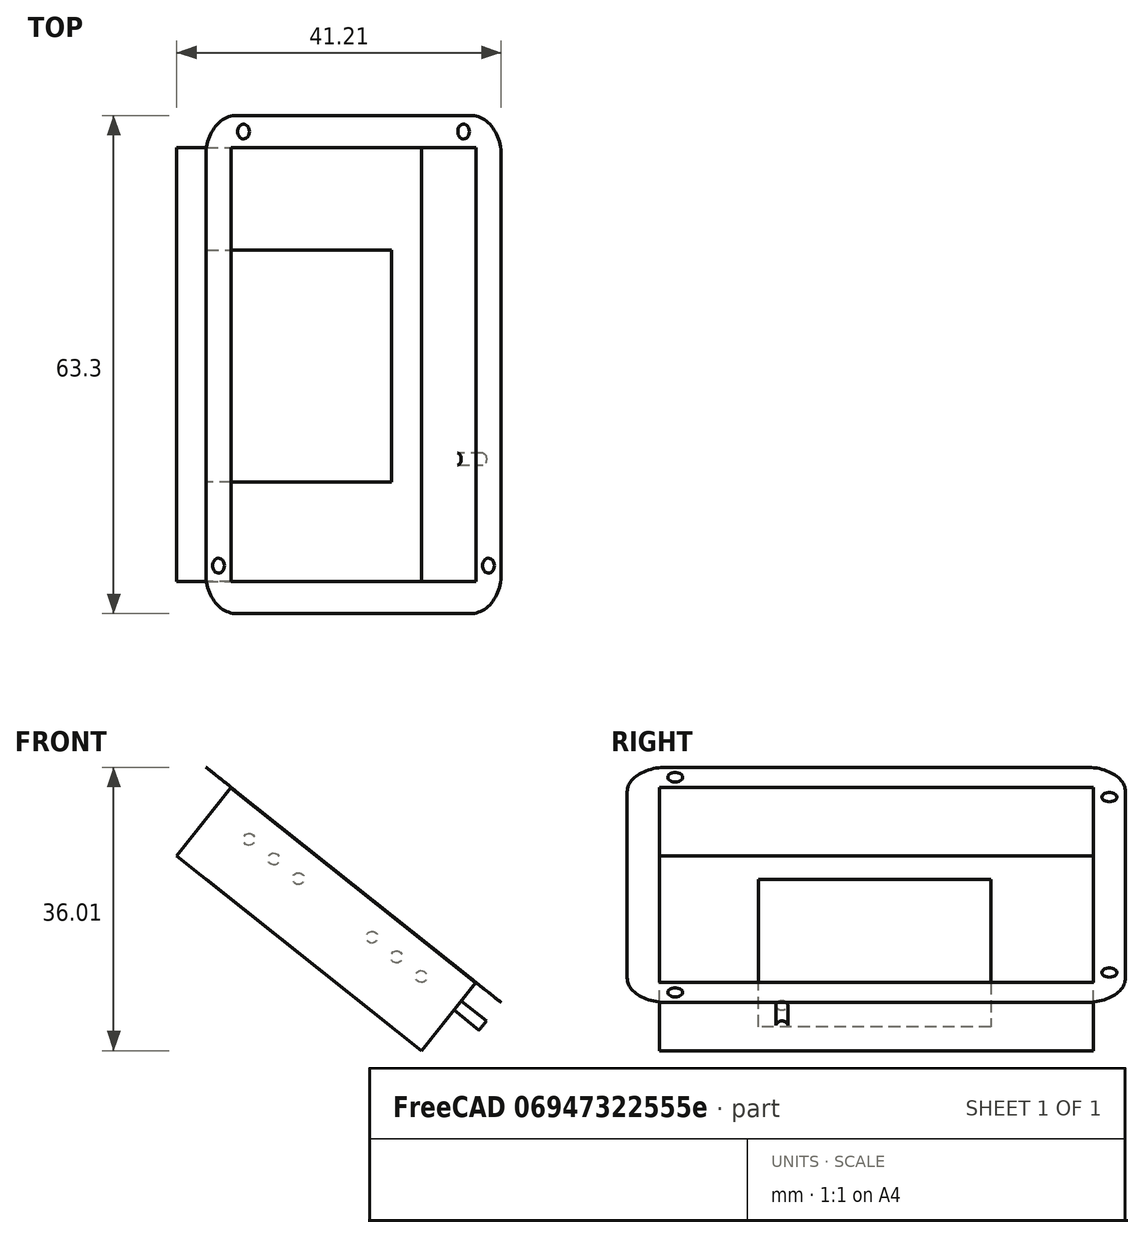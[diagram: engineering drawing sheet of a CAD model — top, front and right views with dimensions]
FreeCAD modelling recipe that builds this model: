
FCSTD DOCUMENT  (FreeCAD 0.20R29410 (Git))
Label: sensor-assembly3
License: All rights reserved
LicenseURL: http://en.wikipedia.org/wiki/All_rights_reserved
objects: Part::FeaturePython×32, App::FeaturePython×17, App::Link×3
note: 31 computed .brp shape members not serialized (recipe doc carries the construction recipe); baked Part::Feature solids carry a one-line shape summary decoded from their .brp
EXTERNAL_REF file=enclosure.FCStd obj=Link
EXTERNAL_REF file=electronics.FCStd obj=Link
EXTERNAL_REF file=cover.FCStd obj=Link

FEATURE [App::Link] Link002  label="enclosure"
  LinkPlacement = pos=(-20.5515,-30.0951,-26.6981) rot=(0,1,0;0.672893rad)
  LinkedObject = -> <external enclosure.FCStd>#Link
  Placement = pos=(-20.5515,-30.0951,-26.6981) rot=(0,1,0;0.672893rad)
  _LinkOwner = 81
FEATURE [App::Link] Link004  label="electronics"
  LinkPlacement = pos=(-19.9282,-30.0951,-25.9161) rot=(0,1,0;0.672893rad)
  LinkedObject = -> <external electronics.FCStd>#Link
  Placement = pos=(-19.9282,-30.0951,-25.9161) rot=(0,1,0;0.672893rad)
  _LinkOwner = 81
FEATURE [App::Link] Link  label="cover"
  LinkPlacement = pos=(-3.91067,-30.0951,-5.81815) rot=(0,-1,0;2.4687rad)
  LinkedObject = -> <external cover.FCStd>#Link
  Placement = pos=(-3.91067,-30.0951,-5.81815) rot=(0,-1,0;2.4687rad)
  _LinkOwner = 81
FEATURE [Part::FeaturePython] Parts  # WARN: FeaturePython — macro-defined, semantics opaque (R4)
  Group = -> [Link002,Link004,Link]
  GroupMode = 0
FEATURE [Part::FeaturePython] Assembly  label="Assembly3"  # WARN: FeaturePython — macro-defined, semantics opaque (R4)
  AutoRelax = true
  BuildShape = 0
  Freeze = false
  Group = -> [Constraints,Elements,Parts]
  Verbose = false
  _SolverType = 1
  _Version = 1
FEATURE [App::FeaturePython] Constraints  # WARN: FeaturePython — macro-defined, semantics opaque (R4)
  Group = -> [Constraint,Constraint001,Constraint002,Constraint003,Constraint004]
  _Version = 1
FEATURE [App::FeaturePython] Elements  # WARN: FeaturePython — macro-defined, semantics opaque (R4)
  Group = -> [_Element001,_Element003,_Element006,_Element008,_Element019,_Element021,_Element023,_Element024,_Element026,_Element028,_Element029,_Element031,_Element032,_Element034,_Element035,_Element036,_Element037,_Element038,_Element039,_Element040,_Element041,_Element042,_Element,_Element043,_Element044,_Element045,_Element046,_Element047,_Element048,_Element049]
FEATURE [Part::FeaturePython] _Element001  # link proxy (typed FeaturePython)
  Detach = false
  LinkTransform = true
  LinkedObject = -> Link002 [Pad001.Face15]
  _Parent = -> Elements
FEATURE [Part::FeaturePython] _Element003  # link proxy (typed FeaturePython)
  Detach = false
  LinkTransform = true
  LinkedObject = -> Link002 [Pad001.Face11]
  _Parent = -> Elements
FEATURE [Part::FeaturePython] _Element006  # link proxy (typed FeaturePython)
  Detach = false
  LinkTransform = true
  LinkedObject = -> Link002 [Pad001.Face13]
  _Parent = -> Elements
FEATURE [Part::FeaturePython] _Element008  # link proxy (typed FeaturePython)
  Detach = false
  LinkTransform = true
  LinkedObject = -> Link002 [Pad001.Face12]
  _Parent = -> Elements
FEATURE [Part::FeaturePython] _Element019  # link proxy (typed FeaturePython)
  Detach = false
  LinkTransform = true
  LinkedObject = -> Link002 [Pocket003.Face23]
  _Parent = -> Elements
FEATURE [Part::FeaturePython] _Element021  # link proxy (typed FeaturePython)
  Detach = false
  LinkTransform = true
  LinkedObject = -> Link002 [Pocket003.Vertex53]
  _Parent = -> Elements
FEATURE [Part::FeaturePython] _Element023  # link proxy (typed FeaturePython)
  Detach = false
  LinkTransform = true
  LinkedObject = -> Link002 [Pocket001.Vertex32]
  _Parent = -> Elements
FEATURE [Part::FeaturePython] _Element024  # link proxy (typed FeaturePython)
  Detach = false
  LinkTransform = true
  LinkedObject = -> Link002 [Pocket001.Vertex28]
  _Parent = -> Elements
FEATURE [Part::FeaturePython] _Element026  # link proxy (typed FeaturePython)
  Detach = false
  LinkTransform = true
  LinkedObject = -> Link002 [Pocket001.Vertex31]
  _Parent = -> Elements
FEATURE [Part::FeaturePython] _Element028  # link proxy (typed FeaturePython)
  Detach = false
  LinkTransform = true
  LinkedObject = -> Link002 [Pocket003.Face46]
  _Parent = -> Elements
FEATURE [Part::FeaturePython] _Element029  # link proxy (typed FeaturePython)
  Detach = false
  LinkTransform = true
  LinkedObject = -> Link002 [Pocket003.Vertex25]
  _Parent = -> Elements
FEATURE [Part::FeaturePython] _Element031  # link proxy (typed FeaturePython)
  Detach = false
  LinkTransform = true
  LinkedObject = -> Link002 [Pocket003.Vertex54]
  _Parent = -> Elements
FEATURE [Part::FeaturePython] _Element032  # link proxy (typed FeaturePython)
  Detach = false
  LinkTransform = true
  LinkedObject = -> Link002 [Pocket003.Vertex26]
  _Parent = -> Elements
FEATURE [Part::FeaturePython] _Element034  # link proxy (typed FeaturePython)
  Detach = false
  LinkTransform = true
  LinkedObject = -> Link002 [Pocket003.Vertex55]
  _Parent = -> Elements
FEATURE [Part::FeaturePython] _Element035  # link proxy (typed FeaturePython)
  Detach = false
  LinkTransform = true
  LinkedObject = -> Link004 [Pad.Face5]
  _Parent = -> Elements
FEATURE [Part::FeaturePython] _Element036  # link proxy (typed FeaturePython)
  Detach = false
  LinkTransform = true
  LinkedObject = -> Link002 [Pocket003.Face22]
  _Parent = -> Elements
FEATURE [Part::FeaturePython] _Element037  # link proxy (typed FeaturePython)
  Detach = false
  LinkTransform = true
  LinkedObject = -> Link002 [Pocket003.Vertex57]
  _Parent = -> Elements
FEATURE [Part::FeaturePython] _Element038  # link proxy (typed FeaturePython)
  Detach = false
  LinkTransform = true
  LinkedObject = -> Link004 [Pad.Vertex1]
  _Parent = -> Elements
FEATURE [Part::FeaturePython] _Element039  # link proxy (typed FeaturePython)
  Detach = false
  LinkTransform = true
  LinkedObject = -> Link004 [Pad.Vertex3]
  _Parent = -> Elements
FEATURE [Part::FeaturePython] _Element040  # link proxy (typed FeaturePython)
  Detach = false
  LinkTransform = true
  LinkedObject = -> Link002 [Pocket003.Vertex58]
  _Parent = -> Elements
FEATURE [Part::FeaturePython] _Element041  # link proxy (typed FeaturePython)
  Detach = false
  LinkTransform = true
  LinkedObject = -> Link002 [Pocket003.Face48]
  _Parent = -> Elements
FEATURE [Part::FeaturePython] _Element042  # link proxy (typed FeaturePython)
  Detach = false
  LinkTransform = true
  LinkedObject = -> Link004 [Pad.Face1]
  _Parent = -> Elements
FEATURE [Part::FeaturePython] _Element  # link proxy (typed FeaturePython)
  Detach = false
  LinkTransform = true
  LinkedObject = -> Link004 [Pad.Face3]
  _Parent = -> Elements
FEATURE [App::FeaturePython] Constraint  label="AxialAlignment"  # WARN: FeaturePython — macro-defined, semantics opaque (R4)
  Angle = 0
  AnglePitch = 0
  AngleRoll = 0
  Disabled = false
  Group = -> [ElementLink,ElementLink001]
  LockAngle = false
  Multiply = false
  _ConstraintType = 36
  _Parent = -> Constraints
FEATURE [App::FeaturePython] ElementLink  label="_Element043"  # link proxy (typed FeaturePython)
  LinkTransform = true
  LinkedObject = -> _Element043
  _Parent = -> Constraint
FEATURE [Part::FeaturePython] _Element043  # link proxy (typed FeaturePython)
  Detach = false
  LinkTransform = true
  LinkedObject = -> Link002 [Pocket004.Face22]
  _Parent = -> Elements
FEATURE [App::FeaturePython] ElementLink001  label="_Element035"  # link proxy (typed FeaturePython)
  LinkTransform = true
  LinkedObject = -> _Element035
  _Parent = -> Constraint
FEATURE [App::FeaturePython] Constraint001  label="Attachment"  # WARN: FeaturePython — macro-defined, semantics opaque (R4)
  Cascade = false
  Disabled = false
  Group = -> [ElementLink002,ElementLink003]
  Multiply = false
  _ConstraintType = 45
  _Parent = -> Constraints
FEATURE [App::FeaturePython] ElementLink002  label="_Element035"  # link proxy (typed FeaturePython)
  LinkTransform = true
  LinkedObject = -> _Element035
  _Parent = -> Constraint001
FEATURE [App::FeaturePython] ElementLink003  label="_Element043"  # link proxy (typed FeaturePython)
  LinkTransform = true
  LinkedObject = -> _Element043
  _Parent = -> Constraint001
FEATURE [App::FeaturePython] Constraint002  label="PointsCoincident"  # WARN: FeaturePython — macro-defined, semantics opaque (R4)
  Disabled = false
  Group = -> [ElementLink004,ElementLink005]
  _ConstraintType = 1
  _Parent = -> Constraints
FEATURE [App::FeaturePython] ElementLink004  label="_Element044"  # link proxy (typed FeaturePython)
  LinkTransform = true
  LinkedObject = -> _Element044
  _Parent = -> Constraint002
FEATURE [Part::FeaturePython] _Element044  # link proxy (typed FeaturePython)
  Detach = false
  LinkTransform = true
  LinkedObject = -> Link [Pad001.Vertex27]
  _Parent = -> Elements
FEATURE [App::FeaturePython] ElementLink005  label="_Element045"  # link proxy (typed FeaturePython)
  LinkTransform = true
  LinkedObject = -> _Element045
  _Parent = -> Constraint002
FEATURE [Part::FeaturePython] _Element045  # link proxy (typed FeaturePython)
  Detach = false
  LinkTransform = true
  LinkedObject = -> Link002 [Pocket004.Vertex56]
  _Parent = -> Elements
FEATURE [App::FeaturePython] Constraint003  label="PointsCoincident001"  # WARN: FeaturePython — macro-defined, semantics opaque (R4)
  Disabled = false
  Group = -> [ElementLink006,ElementLink007]
  _ConstraintType = 1
  _Parent = -> Constraints
FEATURE [App::FeaturePython] ElementLink006  label="_Element046"  # link proxy (typed FeaturePython)
  LinkTransform = true
  LinkedObject = -> _Element046
  _Parent = -> Constraint003
FEATURE [Part::FeaturePython] _Element046  # link proxy (typed FeaturePython)
  Detach = false
  LinkTransform = true
  LinkedObject = -> Link [Pad001.Vertex28]
  _Parent = -> Elements
FEATURE [App::FeaturePython] ElementLink007  label="_Element047"  # link proxy (typed FeaturePython)
  LinkTransform = true
  LinkedObject = -> _Element047
  _Parent = -> Constraint003
FEATURE [Part::FeaturePython] _Element047  # link proxy (typed FeaturePython)
  Detach = false
  LinkTransform = true
  LinkedObject = -> Link002 [Pocket004.Vertex55]
  _Parent = -> Elements
FEATURE [App::FeaturePython] Constraint004  label="PointsCoincident002"  # WARN: FeaturePython — macro-defined, semantics opaque (R4)
  Disabled = false
  Group = -> [ElementLink008,ElementLink009]
  _ConstraintType = 1
  _Parent = -> Constraints
FEATURE [App::FeaturePython] ElementLink008  label="_Element048"  # link proxy (typed FeaturePython)
  LinkTransform = true
  LinkedObject = -> _Element048
  _Parent = -> Constraint004
FEATURE [Part::FeaturePython] _Element048  # link proxy (typed FeaturePython)
  Detach = false
  LinkTransform = true
  LinkedObject = -> Link [Pad001.Vertex7]
  _Parent = -> Elements
FEATURE [App::FeaturePython] ElementLink009  label="_Element049"  # link proxy (typed FeaturePython)
  LinkTransform = true
  LinkedObject = -> _Element049
  _Parent = -> Constraint004
FEATURE [Part::FeaturePython] _Element049  # link proxy (typed FeaturePython)
  Detach = false
  LinkTransform = true
  LinkedObject = -> Link002 [Pocket004.Vertex34]
  _Parent = -> Elements

RESOLVED EXTERNAL PARTS (link-assembly join: the EXTERNAL_REF files above that resolve inside this repo's crawl, each included once):
---- part cover.FCStd = doc fcstd_da3d89a7d0ec ----
FCSTD DOCUMENT  (FreeCAD 0.20R29410 (Git))
Label: cover
License: All rights reserved
LicenseURL: http://en.wikipedia.org/wiki/All_rights_reserved
objects: Sketcher::SketchObject×3, PartDesign::Pad×2, PartDesign::Pocket×1, PartDesign::Body×1, App::Link×1
note: 10 computed .brp shape members not serialized (recipe doc carries the construction recipe); baked Part::Feature solids carry a one-line shape summary decoded from their .brp

FEATURE [Sketcher::SketchObject] Sketch009
  FullyConstrained = false
  MapMode = 5
  Placement = pos=(0,0,12.1) rot=(0,0,1;0rad)
  sketch-geometry (12):
    g0: LineSegment StartX=-18.975 StartY=31.65 StartZ=0 EndX=18.975 EndY=31.65 EndZ=0
    g1: LineSegment StartX=23.975 StartY=26.65 StartZ=0 EndX=23.975 EndY=-26.65 EndZ=0
    g2: LineSegment StartX=18.975 StartY=-31.65 StartZ=0 EndX=-18.975 EndY=-31.65 EndZ=0
    g3: LineSegment StartX=-23.975 StartY=-26.65 StartZ=0 EndX=-23.975 EndY=26.65 EndZ=0
    g4: ArcOfCircle CenterX=-18.975 CenterY=26.65 CenterZ=0 NormalX=0 NormalY=0 NormalZ=1 AngleXU=0 Radius=5 StartAngle=1.5708 EndAngle=3.14159
    g5: ArcOfCircle CenterX=18.975 CenterY=26.65 CenterZ=0 NormalX=0 NormalY=0 NormalZ=1 AngleXU=0 Radius=5 StartAngle=0 EndAngle=1.5708
    g6: ArcOfCircle CenterX=-18.975 CenterY=-26.65 CenterZ=0 NormalX=0 NormalY=0 NormalZ=1 AngleXU=0 Radius=5 StartAngle=3.14159 EndAngle=4.71239
    g7: ArcOfCircle CenterX=18.975 CenterY=-26.65 CenterZ=0 NormalX=0 NormalY=0 NormalZ=1 AngleXU=0 Radius=5 StartAngle=4.71239 EndAngle=6.28319
    g8: Circle CenterX=17.875 CenterY=29.6 CenterZ=0 NormalX=0 NormalY=0 NormalZ=1 AngleXU=0 Radius=1.15
    g9: Circle CenterX=-17.875 CenterY=29.6 CenterZ=0 NormalX=0 NormalY=0 NormalZ=1 AngleXU=0 Radius=1.15
    g10: Circle CenterX=21.925 CenterY=-25.55 CenterZ=0 NormalX=0 NormalY=0 NormalZ=1 AngleXU=0 Radius=1.15
    g11: Circle CenterX=-21.925 CenterY=-25.55 CenterZ=0 NormalX=0 NormalY=0 NormalZ=1 AngleXU=0 Radius=1.15
  constraints (12):
    c: Coincident(g4,g3)
    c: Coincident(g4,g0)
    c: Coincident(g5,g0)
    c: Coincident(g5,g1)
    c: Coincident(g6,g3)
    c: Coincident(g6,g2)
    c: Coincident(g7,g2)
    c: Coincident(g1,g7)
    c: Diameter(g8) = 2.3
    c: Diameter(g9) = 2.3
    c: Diameter(g10) = 2.3
    c: Diameter(g11) = 2.3
FEATURE [PartDesign::Pad] Pad
  Direction = (0,0,1)
  Length = 2.5
  Length2 = 10
  Placement = pos=(0,0,12.1) rot=(0,0,1;0rad)
  Profile = -> Sketch009
  ReferenceAxis = -> Sketch009 [N_Axis]
  Type = 0
FEATURE [Sketcher::SketchObject] Sketch
  ExternalGeometry = -> [Pad]
  FullyConstrained = true
  MapMode = 5
  Placement = pos=(0,0,12.1) rot=(1,0,0;3.14159rad)
  Support = -> [Pad]
  sketch-geometry (4):
    g0: Circle CenterX=21.925 CenterY=25.55 CenterZ=0 NormalX=0 NormalY=0 NormalZ=1 AngleXU=0 Radius=2.125
    g1: Circle CenterX=-21.925 CenterY=25.55 CenterZ=0 NormalX=0 NormalY=0 NormalZ=1 AngleXU=0 Radius=2.125
    g2: Circle CenterX=17.875 CenterY=-29.6 CenterZ=0 NormalX=0 NormalY=0 NormalZ=1 AngleXU=0 Radius=2.125
    g3: Circle CenterX=-17.875 CenterY=-29.6 CenterZ=0 NormalX=0 NormalY=0 NormalZ=1 AngleXU=0 Radius=2.125
  constraints (8):
    c: Coincident(g0,g-3)
    c: Diameter(g0) = 4.25
    c: Diameter(g1) = 4.25
    c: Coincident(g1,g-4)
    c: Coincident(g2,g-5)
    c: Diameter(g2) = 4.25
    c: Diameter(g3) = 4.25
    c: Coincident(g3,g-6)
FEATURE [PartDesign::Pocket] Pocket
  BaseFeature = -> Pad
  Direction = (0,0,1)
  Length = 1.1
  Length2 = 5
  Placement = pos=(0,0,12.1) rot=(0,0,1;0rad)
  Profile = -> Sketch
  ReferenceAxis = -> Sketch [N_Axis]
  Type = 0
FEATURE [Sketcher::SketchObject] Sketch010
  ExternalGeometry = -> [Pocket]
  FullyConstrained = true
  MapMode = 5
  Placement = pos=(0,0,14.6) rot=(0,0,1;0rad)
  Support = -> [Pocket]
  sketch-geometry (16):
    g0: LineSegment StartX=15.575 StartY=27.25 StartZ=0 EndX=19.575 EndY=27.25 EndZ=0
    g1: LineSegment StartX=19.575 StartY=27.25 StartZ=0 EndX=19.575 EndY=22.25 EndZ=0
    g2: LineSegment StartX=19.575 StartY=22.25 StartZ=0 EndX=15.575 EndY=22.25 EndZ=0
    g3: LineSegment StartX=15.575 StartY=22.25 StartZ=0 EndX=15.575 EndY=27.25 EndZ=0
    g4: LineSegment StartX=-15.575 StartY=27.25 StartZ=0 EndX=-19.575 EndY=27.25 EndZ=0
    g5: LineSegment StartX=-19.575 StartY=27.25 StartZ=0 EndX=-19.575 EndY=22.25 EndZ=0
    g6: LineSegment StartX=-19.575 StartY=22.25 StartZ=0 EndX=-15.575 EndY=22.25 EndZ=0
    g7: LineSegment StartX=-15.575 StartY=22.25 StartZ=0 EndX=-15.575 EndY=27.25 EndZ=0
    g8: LineSegment StartX=15.575 StartY=-27.25 StartZ=0 EndX=19.575 EndY=-27.25 EndZ=0
    g9: LineSegment StartX=19.575 StartY=-27.25 StartZ=0 EndX=19.575 EndY=-22.25 EndZ=0
    g10: LineSegment StartX=19.575 StartY=-22.25 StartZ=0 EndX=15.575 EndY=-22.25 EndZ=0
    g11: LineSegment StartX=15.575 StartY=-22.25 StartZ=0 EndX=15.575 EndY=-27.25 EndZ=0
    g12: LineSegment StartX=-15.575 StartY=-27.25 StartZ=0 EndX=-19.575 EndY=-27.25 EndZ=0
    g13: LineSegment StartX=-19.575 StartY=-27.25 StartZ=0 EndX=-19.575 EndY=-22.25 EndZ=0
    g14: LineSegment StartX=-19.575 StartY=-22.25 StartZ=0 EndX=-15.575 EndY=-22.25 EndZ=0
    g15: LineSegment StartX=-15.575 StartY=-22.25 StartZ=0 EndX=-15.575 EndY=-27.25 EndZ=0
  constraints (48):
    c: Coincident(g0,g1)
    c: Coincident(g1,g2)
    c: Coincident(g2,g3)
    c: Coincident(g3,g0)
    c: Horizontal(g0)
    c: Horizontal(g2)
    c: Vertical(g1)
    c: Vertical(g3)
    c: DistanceY(g1,g1) = 5
    c: DistanceX(g0,g0) = 4
    c: DistanceX(g0,g-4) = 4.4
    c: DistanceY(g0,g-3) = 4.4
    c: Coincident(g4,g5)
    c: Coincident(g5,g6)
    c: Coincident(g6,g7)
    c: Coincident(g7,g4)
    c: Horizontal(g4)
    c: Horizontal(g6)
    c: Vertical(g5)
    c: Vertical(g7)
    c: DistanceY(g4,g-3) = 4.4
    c: DistanceX(g-5,g4) = 4.4
    c: Equal(g7,g3)
    c: Equal(g4,g2)
    c: Coincident(g8,g9)
    c: Coincident(g9,g10)
    c: Coincident(g10,g11)
    c: Coincident(g11,g8)
    c: Horizontal(g8)
    c: Horizontal(g10)
    c: Vertical(g9)
    c: Vertical(g11)
    c: Coincident(g12,g13)
    c: Coincident(g13,g14)
    c: Coincident(g14,g15)
    c: Coincident(g15,g12)
    c: Horizontal(g12)
    c: Horizontal(g14)
    c: Vertical(g13)
    c: Vertical(g15)
    c: Equal(g15,g11)
    c: Equal(g12,g10)
    c: DistanceX(g8,g-4) = 4.4
    c: DistanceY(g-6,g8) = 4.4
    c: Equal(g2,g10)
    c: Equal(g11,g3)
    c: DistanceX(g-5,g12) = 4.4
    c: DistanceY(g-6,g12) = 4.4
FEATURE [PartDesign::Pad] Pad001
  BaseFeature = -> Pocket
  Direction = (0,0,1)
  Length = 9.75
  Length2 = 10
  Placement = pos=(0,0,12.1) rot=(0,0,1;0rad)
  Profile = -> Sketch010
  ReferenceAxis = -> Sketch010 [N_Axis]
  Type = 0
FEATURE [PartDesign::Body] Body  label="cover"
  Group = -> [Sketch009,Pad,Sketch,Pocket,Sketch010,Pad001]
  Origin = -> Origin
  Tip = -> Pad001
FEATURE [App::Link] Link  label="cover001"
  LinkedObject = -> Body
---- part electronics.FCStd = doc fcstd_a27a320ab60b ----
FCSTD DOCUMENT  (FreeCAD 0.20R29410 (Git))
Label: electronics
License: All rights reserved
LicenseURL: http://en.wikipedia.org/wiki/All_rights_reserved
objects: Sketcher::SketchObject×1, PartDesign::Pad×1, PartDesign::Body×1, App::Link×1
note: 4 computed .brp shape members not serialized (recipe doc carries the construction recipe); baked Part::Feature solids carry a one-line shape summary decoded from their .brp

FEATURE [Sketcher::SketchObject] Sketch
  FullyConstrained = true
  MapMode = 5
  Support = -> [XY_Plane]
  sketch-geometry (4):
    g0: LineSegment StartX=-19.875 StartY=27.55 StartZ=0 EndX=19.875 EndY=27.55 EndZ=0
    g1: LineSegment StartX=19.875 StartY=27.55 StartZ=0 EndX=19.875 EndY=-27.55 EndZ=0
    g2: LineSegment StartX=19.875 StartY=-27.55 StartZ=0 EndX=-19.875 EndY=-27.55 EndZ=0
    g3: LineSegment StartX=-19.875 StartY=-27.55 StartZ=0 EndX=-19.875 EndY=27.55 EndZ=0
  constraints (10):
    c: Coincident(g0,g1)
    c: Coincident(g1,g2)
    c: Coincident(g2,g3)
    c: Coincident(g3,g0)
    c: Horizontal(g2)
    c: Vertical(g1)
    c: DistanceY(g1,g1) = 55.1
    c: DistanceX(g0,g0) = 39.75
    c: Symmetric(g0,g0,g-2)
    c: Symmetric(g2,g0,g-1)
FEATURE [PartDesign::Pad] Pad  label="pad"
  Direction = (0,0,1)
  Length = 11
  Length2 = 10
  Profile = -> Sketch
  ReferenceAxis = -> Sketch [N_Axis]
  Type = 0
FEATURE [PartDesign::Body] Body  label="electronics"
  Group = -> [Sketch,Pad]
  Origin = -> Origin
  Tip = -> Pad
FEATURE [App::Link] Link  label="electronics001"
  LinkedObject = -> Body
---- part enclosure.FCStd = doc fcstd_24d389eb9eb0 ----
FCSTD DOCUMENT  (FreeCAD 0.20R29410 (Git))
Label: enclosure
License: All rights reserved
LicenseURL: http://en.wikipedia.org/wiki/All_rights_reserved
objects: Sketcher::SketchObject×7, PartDesign::Pocket×5, PartDesign::Pad×2, PartDesign::Fillet×2, App::Link×1, PartDesign::Body×1
note: 26 computed .brp shape members not serialized (recipe doc carries the construction recipe); baked Part::Feature solids carry a one-line shape summary decoded from their .brp

FEATURE [Sketcher::SketchObject] Sketch
  FullyConstrained = true
  MapMode = 5
  Support = -> [XY_Plane]
  sketch-geometry (4):
    g0: LineSegment StartX=-23.975 StartY=31.65 StartZ=0 EndX=23.975 EndY=31.65 EndZ=0
    g1: LineSegment StartX=23.975 StartY=31.65 StartZ=0 EndX=23.975 EndY=-31.65 EndZ=0
    g2: LineSegment StartX=23.975 StartY=-31.65 StartZ=0 EndX=-23.975 EndY=-31.65 EndZ=0
    g3: LineSegment StartX=-23.975 StartY=-31.65 StartZ=0 EndX=-23.975 EndY=31.65 EndZ=0
  constraints (10):
    c: Coincident(g0,g1)
    c: Coincident(g1,g2)
    c: Coincident(g2,g3)
    c: Coincident(g3,g0)
    c: Horizontal(g0)
    c: Vertical(g3)
    c: DistanceX(g2,g2) = 47.95
    c: Symmetric(g2,g1,g-2)
    c: DistanceY(g1,g1) = 63.3
    c: Symmetric(g0,g1,g-1)
FEATURE [PartDesign::Pad] Pad
  Direction = (0,0,1)
  Length = 1
  Length2 = 10
  Profile = -> Sketch
  ReferenceAxis = -> Sketch [N_Axis]
  Type = 0
FEATURE [Sketcher::SketchObject] Sketch001
  ExternalGeometry = -> [Pad]
  FullyConstrained = true
  MapMode = 5
  Placement = pos=(0,0,1) rot=(0,0,1;0rad)
  Support = -> [Pad]
  sketch-geometry (8):
    g0: LineSegment StartX=-19.925 StartY=27.6 StartZ=0 EndX=19.925 EndY=27.6 EndZ=0
    g1: LineSegment StartX=19.925 StartY=27.6 StartZ=0 EndX=19.925 EndY=-27.6 EndZ=0
    g2: LineSegment StartX=19.925 StartY=-27.6 StartZ=0 EndX=-19.925 EndY=-27.6 EndZ=0
    g3: LineSegment StartX=-19.925 StartY=-27.6 StartZ=0 EndX=-19.925 EndY=27.6 EndZ=0
    g4: LineSegment StartX=-23.975 StartY=31.65 StartZ=0 EndX=23.975 EndY=31.65 EndZ=0
    g5: LineSegment StartX=23.975 StartY=31.65 StartZ=0 EndX=23.975 EndY=-31.65 EndZ=0
    g6: LineSegment StartX=23.975 StartY=-31.65 StartZ=0 EndX=-23.975 EndY=-31.65 EndZ=0
    g7: LineSegment StartX=-23.975 StartY=-31.65 StartZ=0 EndX=-23.975 EndY=31.65 EndZ=0
  constraints (20):
    c: Coincident(g0,g1)
    c: Coincident(g1,g2)
    c: Coincident(g2,g3)
    c: Coincident(g3,g0)
    c: Horizontal(g0)
    c: Vertical(g1)
    c: Coincident(g4,g5)
    c: Coincident(g5,g6)
    c: Coincident(g6,g7)
    c: Coincident(g7,g4)
    c: Horizontal(g4)
    c: Horizontal(g6)
    c: Vertical(g5)
    c: Vertical(g7)
    c: Coincident(g4,g-3)
    c: Coincident(g5,g-4)
    c: Symmetric(g2,g1,g-2)
    c: Symmetric(g0,g2,g-1)
    c: DistanceX(g1,g5) = 4.05
    c: DistanceY(g5,g1) = 4.05
FEATURE [PartDesign::Pad] Pad001
  BaseFeature = -> Pad
  Direction = (0,0,1)
  Length = 11.1
  Length2 = 10
  Profile = -> Sketch001
  ReferenceAxis = -> Sketch001 [N_Axis]
  Type = 0
FEATURE [App::Link] Link  label="enclosure001"
  LinkedObject = -> Body
FEATURE [Sketcher::SketchObject] Sketch003
  ExternalGeometry = -> [Pad001]
  FullyConstrained = true
  MapMode = 5
  Placement = pos=(0,0,1) rot=(0,0,1;0rad)
  sketch-geometry (4):
    g0: LineSegment StartX=-15 StartY=14.6 StartZ=0 EndX=15 EndY=14.6 EndZ=0
    g1: LineSegment StartX=15 StartY=14.6 StartZ=0 EndX=15 EndY=-14.9 EndZ=0
    g2: LineSegment StartX=15 StartY=-14.9 StartZ=0 EndX=-15 EndY=-14.9 EndZ=0
    g3: LineSegment StartX=-15 StartY=-14.9 StartZ=0 EndX=-15 EndY=14.6 EndZ=0
  constraints (12):
    c: Coincident(g0,g1)
    c: Coincident(g1,g2)
    c: Coincident(g2,g3)
    c: Coincident(g3,g0)
    c: Horizontal(g2)
    c: Vertical(g1)
    c: Vertical(g3)
    c: DistanceX(g0,g0) = 30
    c: DistanceY(g1,g1) = 29.5
    c: DistanceX(g-1,g0) = 15
    c: Horizontal(g0)
    c: DistanceY(g0,g-3) = 13
FEATURE [PartDesign::Pocket] Pocket
  BaseFeature = -> Pad001
  Direction = (0,0,-1)
  Length = 0
  Length2 = 5
  Profile = -> Sketch003
  ReferenceAxis = -> Sketch003 [N_Axis]
  Type = 3
  UpToFace = -> Pad001 [Face4]
FEATURE [PartDesign::Fillet] Fillet
  Base = -> Pocket [Edge22,Edge8,Edge20,Edge5,Edge16,Edge1,Edge17,Edge2]
  BaseFeature = -> Pocket
  Radius = 5
  SupportTransform = false
  UseAllEdges = false
FEATURE [PartDesign::Fillet] Fillet001
  Base = -> Fillet [Edge1,Edge5,Edge7]
  BaseFeature = -> Fillet
  Radius = 1.99
  SupportTransform = false
  UseAllEdges = false
FEATURE [Sketcher::SketchObject] Sketch005
  ExternalGeometry = -> [Fillet001]
  FullyConstrained = true
  MapMode = 5
  Placement = pos=(0,0,12.1) rot=(0,0,1;0rad)
  Support = -> [Fillet001]
  sketch-geometry (4):
    g0: Circle CenterX=17.925 CenterY=29.6 CenterZ=0 NormalX=0 NormalY=0 NormalZ=1 AngleXU=0 Radius=0.95
    g1: Circle CenterX=-17.925 CenterY=29.6 CenterZ=0 NormalX=0 NormalY=0 NormalZ=1 AngleXU=0 Radius=0.95
    g2: Circle CenterX=21.925 CenterY=-25.6 CenterZ=0 NormalX=0 NormalY=0 NormalZ=1 AngleXU=0 Radius=0.95
    g3: Circle CenterX=-21.925 CenterY=-25.6 CenterZ=0 NormalX=0 NormalY=0 NormalZ=1 AngleXU=0 Radius=0.95
  constraints (13):
    c: Diameter(g0) = 1.9
    c: DistanceY(g-3,g-5) = 4.05
    c: DistanceY(g-3,g1) = 2
    c: DistanceX(g-3,g1) = 2
    c: Equal(g1,g0)
    c: DistanceY(g-6,g0) = 2
    c: DistanceX(g0,g-8) = 2
    c: Diameter(g2) = 1.9
    c: DistanceX(g-8,g2) = 2
    c: DistanceY(g-8,g2) = 2
    c: Diameter(g3) = 1.9
    c: DistanceX(g3,g-9) = 2
    c: DistanceY(g-9,g3) = 2
FEATURE [PartDesign::Pocket] Pocket001
  BaseFeature = -> Fillet001
  Direction = (0,0,-1)
  Length = 10
  Length2 = 5
  Profile = -> Sketch005
  ReferenceAxis = -> Sketch005 [N_Axis]
  Type = 0
FEATURE [Sketcher::SketchObject] Sketch006
  AttachmentOffset = pos=(0,-2,0) rot=(0,0,1;0rad)
  ExternalGeometry = -> [Pocket001]
  FullyConstrained = false
  MapMode = 5
  Placement = pos=(23.975,0,-2) rot=(0.57735,0.57735,0.57735;2.0944rad)
  Support = -> [Pocket001]
  sketch-geometry (11):
    g0: Circle CenterX=16 CenterY=10.35 CenterZ=0 NormalX=0 NormalY=0 NormalZ=1 AngleXU=0 Radius=0.75
    g1: LineSegment StartX=31.0335 StartY=10.35 StartZ=0 EndX=-29.8986 EndY=10.35 EndZ=0
    g2: Circle CenterX=12 CenterY=10.35 CenterZ=0 NormalX=0 NormalY=0 NormalZ=1 AngleXU=0 Radius=0.75
    g3: Circle CenterX=4 CenterY=10.35 CenterZ=0 NormalX=0 NormalY=0 NormalZ=1 AngleXU=0 Radius=0.75
    g4: Circle CenterX=8 CenterY=10.35 CenterZ=0 NormalX=0 NormalY=0 NormalZ=1 AngleXU=0 Radius=0.75
    g5: LineSegment StartX=-6.35 StartY=11.7225 StartZ=0 EndX=-6.35 EndY=9.03689 EndZ=0
    g6: Circle CenterX=-4 CenterY=10.35 CenterZ=0 NormalX=0 NormalY=0 NormalZ=1 AngleXU=0 Radius=0.75
    g7: Circle CenterX=0 CenterY=10.35 CenterZ=0 NormalX=0 NormalY=0 NormalZ=1 AngleXU=0 Radius=0.75
    g8: Circle CenterX=-12 CenterY=10.35 CenterZ=0 NormalX=0 NormalY=0 NormalZ=1 AngleXU=0 Radius=0.75
    g9: Circle CenterX=-8 CenterY=10.35 CenterZ=0 NormalX=0 NormalY=0 NormalZ=1 AngleXU=0 Radius=0.75
    g10: Circle CenterX=-16 CenterY=10.35 CenterZ=0 NormalX=0 NormalY=0 NormalZ=1 AngleXU=0 Radius=0.75
  constraints (30):
    c: Diameter(g0) = 1.5
    c: Horizontal(g1)
    c: PointOnObject(g0,g1)
    c: PointOnObject(g2,g1)
    c: PointOnObject(g4,g1)
    c: Vertical(g5)
    c: DistanceX(g3,g4) = 4
    c: DistanceX(g4,g2) = 4
    c: DistanceX(g2,g0) = 4
    c: PointOnObject(g3,g1)
    c: DistanceX(g6,g7) = 4
    c: PointOnObject(g7,g1)
    c: DistanceX(g7,g3) = 4
    c: PointOnObject(g6,g1)
    c: PointOnObject(g8,g1)
    c: Equal(g6,g7)
    c: Equal(g7,g3)
    c: Equal(g3,g4)
    c: Equal(g4,g2)
    c: Equal(g2,g0)
    c: PointOnObject(g9,g1)
    c: Equal(g9,g0)
    c: DistanceX(g9,g6) = 4
    c: DistanceX(g8,g9) = 4
    c: Equal(g8,g0)
    c: PointOnObject(g10,g1)
    c: DistanceX(g10,g8) = 4
    c: Equal(g10,g0)
    c: DistanceY(g1,g-3) = 3.75
    c: PointOnObject(g7,g-2)
FEATURE [PartDesign::Pocket] Pocket002
  BaseFeature = -> Pocket001
  Direction = (-1,0,0)
  Length = 0
  Length2 = 5
  Profile = -> Sketch006
  ReferenceAxis = -> Sketch006 [N_Axis]
  Type = 1
FEATURE [Sketcher::SketchObject] Sketch007
  ExternalGeometry = -> [Pocket002]
  FullyConstrained = false
  MapMode = 5
  Placement = pos=(0,31.65,0) rot=(0,0.707107,0.707107;3.14159rad)
  Support = -> [Pocket002]
  sketch-geometry (7):
    g0: LineSegment StartX=-20.9174 StartY=8.35 StartZ=0 EndX=22.0003 EndY=8.35 EndZ=0
    g1: Circle CenterX=9.975 CenterY=8.35 CenterZ=0 NormalX=0 NormalY=0 NormalZ=1 AngleXU=0 Radius=0.75
    g2: Circle CenterX=5.975 CenterY=8.35 CenterZ=0 NormalX=0 NormalY=0 NormalZ=1 AngleXU=0 Radius=0.75
    g3: Circle CenterX=-13.975 CenterY=8.35 CenterZ=0 NormalX=0 NormalY=0 NormalZ=1 AngleXU=0 Radius=0.75
    g4: Circle CenterX=-9.975 CenterY=8.35 CenterZ=0 NormalX=0 NormalY=0 NormalZ=1 AngleXU=0 Radius=0.75
    g5: Circle CenterX=-5.975 CenterY=8.35 CenterZ=0 NormalX=0 NormalY=0 NormalZ=1 AngleXU=0 Radius=0.75
    g6: Circle CenterX=13.975 CenterY=8.35 CenterZ=0 NormalX=0 NormalY=0 NormalZ=1 AngleXU=0 Radius=0.75
  constraints (20):
    c: Horizontal(g0)
    c: PointOnObject(g1,g0)
    c: PointOnObject(g2,g0)
    c: DistanceX(g2,g1) = 4
    c: DistanceX(g3,g4) = 4
    c: DistanceX(g4,g5) = 4
    c: PointOnObject(g4,g0)
    c: PointOnObject(g5,g0)
    c: PointOnObject(g3,g0)
    c: Equal(g3,g4)
    c: Equal(g4,g5)
    c: Equal(g1,g2)
    c: PointOnObject(g6,g0)
    c: DistanceX(g1,g6) = 4
    c: Radius(g5) = 0.75
    c: Equal(g3,g6)
    c: Equal(g6,g1)
    c: DistanceY(g0,g-3) = 3.75
    c: DistanceX(g6,g-3) = 5
    c: DistanceX(g-3,g3) = 5
FEATURE [PartDesign::Pocket] Pocket003
  BaseFeature = -> Pocket002
  Direction = (0,-1,2e-16)
  Length = 0
  Length2 = 5
  Profile = -> Sketch007
  ReferenceAxis = -> Sketch007 [N_Axis]
  Type = 2
FEATURE [Sketcher::SketchObject] Sketch008
  ExternalGeometry = -> [Pocket003]
  FullyConstrained = false
  MapMode = 5
  Placement = pos=(0,-31.65,0) rot=(1,0,0;1.5708rad)
  Support = -> [Pocket003]
  sketch-geometry (5):
    g0: LineSegment StartX=5.975 StartY=15.6614 StartZ=0 EndX=5.975 EndY=-1.54377 EndZ=0
    g1: LineSegment StartX=-3.025 StartY=14.1 StartZ=0 EndX=14.975 EndY=14.1 EndZ=0
    g2: LineSegment StartX=14.975 StartY=14.1 StartZ=0 EndX=14.975 EndY=2.99 EndZ=0
    g3: LineSegment StartX=14.975 StartY=2.99 StartZ=0 EndX=-3.025 EndY=2.99 EndZ=0
    g4: LineSegment StartX=-3.025 StartY=2.99 StartZ=0 EndX=-3.025 EndY=14.1 EndZ=0
  constraints (13):
    c: DistanceX(g0,g-3) = 13
    c: Vertical(g0)
    c: Coincident(g1,g2)
    c: Coincident(g2,g3)
    c: Coincident(g3,g4)
    c: Coincident(g4,g1)
    c: Horizontal(g3)
    c: Vertical(g2)
    c: Vertical(g4)
    c: DistanceX(g1,g1) = 18
    c: Symmetric(g1,g1,g0)
    c: DistanceY(g-3,g1) = 2
    c: DistanceY(g-4,g2) = 1
FEATURE [PartDesign::Pocket] Pocket004
  BaseFeature = -> Pocket003
  Direction = (0,1,-2e-16)
  Length = 5
  Length2 = 5
  Profile = -> Sketch008
  ReferenceAxis = -> Sketch008 [N_Axis]
  Type = 2
FEATURE [PartDesign::Body] Body  label="enclosure"
  Group = -> [Sketch,Pad,Sketch001,Pad001,Sketch003,Pocket,Fillet,Fillet001,Sketch005,Pocket001,Sketch006,Pocket002,Sketch007,Pocket003,Sketch008,Pocket004]
  Origin = -> Origin
  Tip = -> Pocket004
